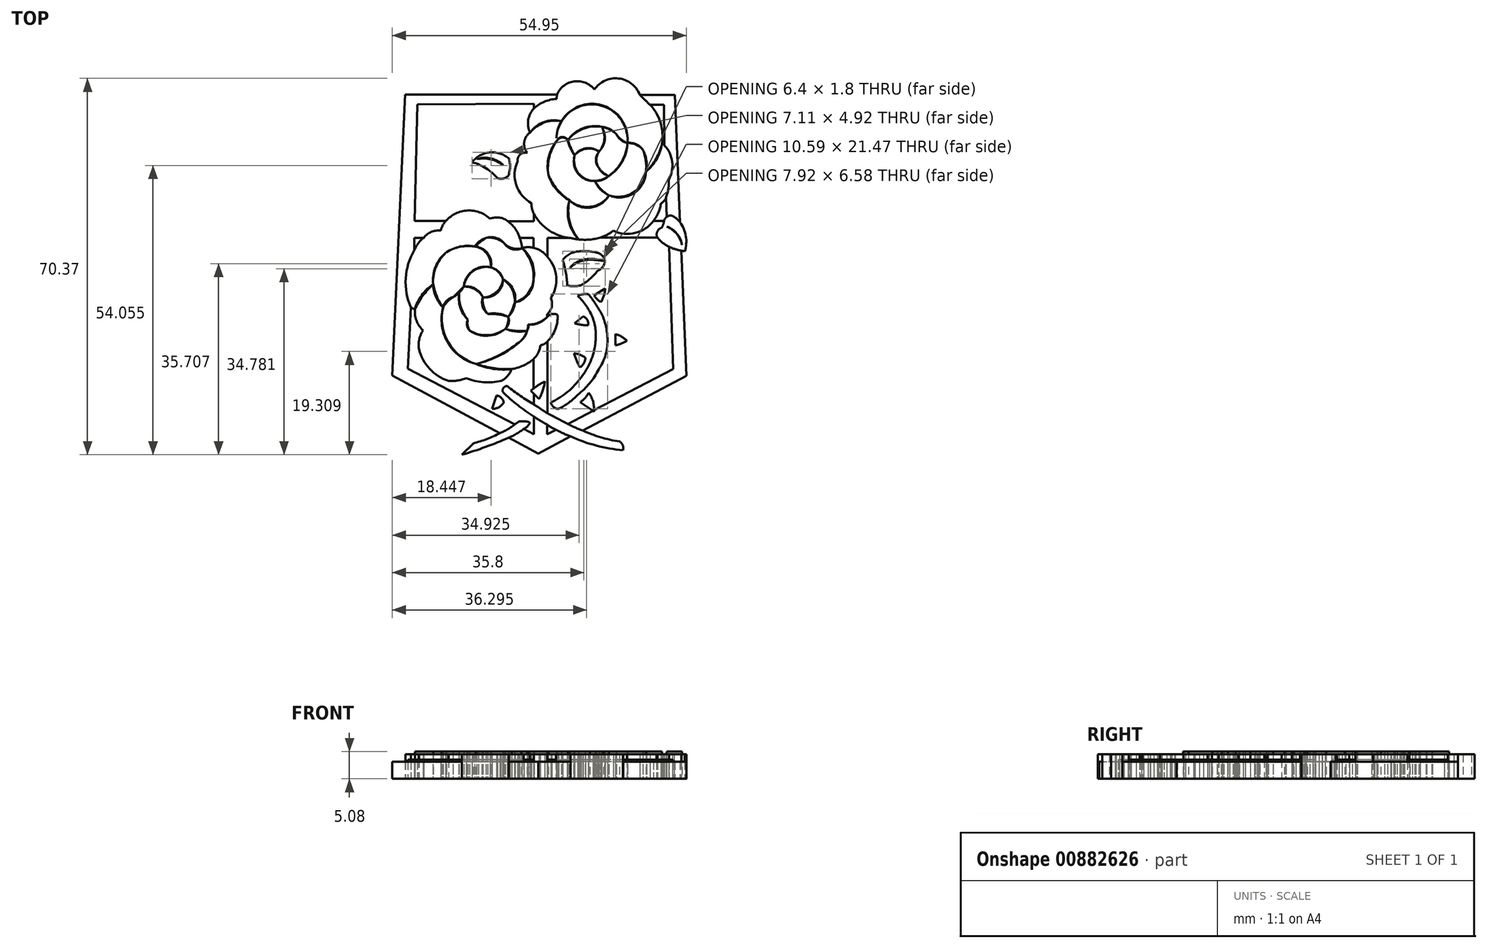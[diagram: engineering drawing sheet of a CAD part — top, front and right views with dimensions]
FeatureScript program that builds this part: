
annotation { "Feature Type Name" : "Feature", "Feature Type Description" : "" }
export const myFeature = defineFeature(function(context is Context, id is Id, definition is map)
    precondition{}
    {
        {
            var Q0;
            Q0=qCreatedBy(makeId("Top.planeOp"),FACE);
            var sketch = newSketch(context, id + "F0", { "sketchPlane" : qUnion([Q0])});
            skLineSegment(sketch, "E0", {"start": v(26.78, -3.75) * mm, "end": v(27.69, -27.16) * mm});
            skLineSegment(sketch, "E1", {"start": v(27.69, -27.16) * mm, "end": v(8.33, -37.36) * mm});
            skLineSegment(sketch, "E2", {"start": v(6.03, -38.47) * mm, "end": v(0, -41.69) * mm});
            skLineSegment(sketch, "E3", {"start": v(0, -41.69) * mm, "end": v(-5.51, -38.69) * mm});
            skLineSegment(sketch, "E4", {"start": v(-7.15, -37.85) * mm, "end": v(-27.26, -27.07) * mm});
            skLineSegment(sketch, "E5", {"start": v(-27.26, -27.07) * mm, "end": v(-24.88, 25.46) * mm});
            skLineSegment(sketch, "E6", {"start": v(-24.88, 25.46) * mm, "end": v(3.53, 25.46) * mm});
            skLineSegment(sketch, "E7", {"start": v(18.98, 25.4) * mm, "end": v(25.53, 25.4) * mm});
            skLineSegment(sketch, "E8", {"start": v(25.53, 25.4) * mm, "end": v(26.49, 1.59) * mm});
            skLineSegment(sketch, "E9", {"start": v(21.57, 1.85) * mm, "end": v(23.52, 1.85) * mm});
            skLineSegment(sketch, "E10", {"start": v(24.05, 2.58) * mm, "end": v(23.9, 6.24) * mm});
            skLineSegment(sketch, "E11", {"start": v(23.5, 23.55) * mm, "end": v(23.6, 15.95) * mm});
            skLineSegment(sketch, "E12", {"start": v(23.5, 23.55) * mm, "end": v(20.94, 23.52) * mm});
            skLineSegment(sketch, "E13", {"start": v(-0.83, 22.84) * mm, "end": v(-0.83, 23.76) * mm});
            skLineSegment(sketch, "E14", {"start": v(-0.83, 23.76) * mm, "end": v(-22.6, 23.6) * mm});
            skLineSegment(sketch, "E15", {"start": v(-22.6, 23.6) * mm, "end": v(-23.11, 1.83) * mm});
            skLineSegment(sketch, "E16", {"start": v(-23.11, 1.83) * mm, "end": v(-17.24, 1.83) * mm});
            skLineSegment(sketch, "E17", {"start": v(-23.15, -3.63) * mm, "end": v(-23.15, -1.32) * mm});
            skLineSegment(sketch, "E18", {"start": v(-23.15, -1.32) * mm, "end": v(-21.4, -1.32) * mm});
            skLineSegment(sketch, "E19", {"start": v(-5.67, 1.77) * mm, "end": v(-0.84, 1.77) * mm});
            skLineSegment(sketch, "E20", {"start": v(-0.84, 1.77) * mm, "end": v(-0.84, 3.19) * mm});
            skLineSegment(sketch, "E21", {"start": v(-3.46, -1.35) * mm, "end": v(-0.86, -1.35) * mm});
            skLineSegment(sketch, "E22", {"start": v(-0.86, -1.35) * mm, "end": v(-0.86, -3.22) * mm});
            skLineSegment(sketch, "E23", {"start": v(1.7, -4.9) * mm, "end": v(1.7, -1.37) * mm});
            skLineSegment(sketch, "E24", {"start": v(1.7, -1.37) * mm, "end": v(6.1, -1.37) * mm});
            skLineSegment(sketch, "E25", {"start": v(11.62, -1.3) * mm, "end": v(22.3, -1.3) * mm});
            skLineSegment(sketch, "E26", {"start": v(24.48, -3) * mm, "end": v(25.26, -25.87) * mm});
            skLineSegment(sketch, "E27", {"start": v(25.26, -25.87) * mm, "end": v(10.43, -33.58) * mm});
            skLineSegment(sketch, "E28", {"start": v(10.23, -33.7) * mm, "end": v(5.57, -36.14) * mm});
            skLineSegment(sketch, "E29", {"start": v(3.32, -37.22) * mm, "end": v(1.68, -38.07) * mm});
            skLineSegment(sketch, "E30", {"start": v(1.68, -38.07) * mm, "end": v(1.68, -36.26) * mm});
            skLineSegment(sketch, "E31", {"start": v(-0.82, -34.75) * mm, "end": v(-0.82, -38.03) * mm});
            skLineSegment(sketch, "E32", {"start": v(-0.82, -38.03) * mm, "end": v(-2.68, -37.02) * mm});
            skLineSegment(sketch, "E33", {"start": v(-4.38, -36.22) * mm, "end": v(-24.37, -25.83) * mm});
            skLineSegment(sketch, "E34", {"start": v(-24.37, -25.83) * mm, "end": v(-23.8, -14.36) * mm});
            skLineSegment(sketch, "E35", {"start": v(1.72, -34.13) * mm, "end": v(1.72, -20.72) * mm});
            skLineSegment(sketch, "E36", {"start": v(-0.84, -24) * mm, "end": v(-0.84, -29.51) * mm});
            skLineSegment(sketch, "E37", {"start": v(-0.8, -30.52) * mm, "end": v(-0.8, -32.5) * mm});
            skArc(sketch, "E38", {"start": v(5.57, -36.14) * mm, "mid": v(6.92, -36.8) * mm, "end": v(8.33, -37.36) * mm});
            skArc(sketch, "E39", {"start": v(3.32, -37.22) * mm, "mid": v(4.67, -37.87) * mm, "end": v(6.03, -38.47) * mm});
            skArc(sketch, "E40", {"start": v(6.03, -38.47) * mm, "mid": v(10.84, -40.16) * mm, "end": v(15.85, -41.06) * mm});
            skArc(sketch, "E41", {"start": v(8.33, -37.36) * mm, "mid": v(11.7, -38.63) * mm, "end": v(15.2, -39.4) * mm});
            skArc(sketch, "E42", {"start": v(15.85, -41.06) * mm, "mid": v(15.8, -40.13) * mm, "end": v(15.2, -39.4) * mm});
            skLineSegment(sketch, "E43", {"start": v(7.86, -32.07) * mm, "end": v(10.23, -33.7) * mm});
            skLineSegment(sketch, "E44", {"start": v(10.23, -33.7) * mm, "end": v(10.44, -33.84) * mm});
            skLineSegment(sketch, "E45", {"start": v(10.44, -33.84) * mm, "end": v(10.43, -33.58) * mm});
            skArc(sketch, "E46", {"start": v(10.43, -33.58) * mm, "mid": v(10.23, -31.85) * mm, "end": v(9.44, -30.29) * mm});
            skArc(sketch, "E47", {"start": v(7.86, -32.07) * mm, "mid": v(8.76, -31.28) * mm, "end": v(9.44, -30.29) * mm});
            skArc(sketch, "E48", {"start": v(22.3, -1.3) * mm, "mid": v(23.29, -2.28) * mm, "end": v(24.48, -3) * mm});
            skArc(sketch, "E49", {"start": v(24.48, -3) * mm, "mid": v(25.6, -3.46) * mm, "end": v(26.78, -3.75) * mm});
            skArc(sketch, "E50", {"start": v(27.4, -3.88) * mm, "mid": v(27.1, -3.8) * mm, "end": v(26.78, -3.75) * mm});
            skArc(sketch, "E51", {"start": v(27.4, -3.88) * mm, "mid": v(27.6, -1.03) * mm, "end": v(26.49, 1.59) * mm});
            skArc(sketch, "E52", {"start": v(25.4, 2.58) * mm, "mid": v(24.72, 2.82) * mm, "end": v(24.05, 2.58) * mm});
            skArc(sketch, "E53", {"start": v(26.49, 1.59) * mm, "mid": v(25.99, 2.14) * mm, "end": v(25.4, 2.58) * mm});
            skArc(sketch, "E54", {"start": v(24.05, 2.58) * mm, "mid": v(23.71, 2.27) * mm, "end": v(23.52, 1.85) * mm});
            skArc(sketch, "E55", {"start": v(23.09, 0.55) * mm, "mid": v(23.37, 1.17) * mm, "end": v(23.52, 1.85) * mm});
            skArc(sketch, "E56", {"start": v(23.09, 0.55) * mm, "mid": v(22.25, -0.18) * mm, "end": v(22.3, -1.3) * mm});
            skArc(sketch, "E57", {"start": v(26.9, -2.71) * mm, "mid": v(25.96, -0.57) * mm, "end": v(24.05, 0.77) * mm});
            skArc(sketch, "E58", {"start": v(1.68, -36.26) * mm, "mid": v(2.47, -36.8) * mm, "end": v(3.32, -37.22) * mm});
            skArc(sketch, "E59", {"start": v(-0.82, -34.75) * mm, "mid": v(0.41, -35.54) * mm, "end": v(1.68, -36.26) * mm});
            skArc(sketch, "E60", {"start": v(-6.6, -30.2) * mm, "mid": v(-3.82, -32.62) * mm, "end": v(-0.82, -34.75) * mm});
            skArc(sketch, "E61", {"start": v(-5.78, -29.05) * mm, "mid": v(-6.5, -29.4) * mm, "end": v(-6.6, -30.2) * mm});
            skArc(sketch, "E62", {"start": v(-5.78, -29.05) * mm, "mid": v(-3.35, -30.88) * mm, "end": v(-0.8, -32.5) * mm});
            skArc(sketch, "E63", {"start": v(1.72, -34.13) * mm, "mid": v(0.47, -33.31) * mm, "end": v(-0.8, -32.5) * mm});
            skArc(sketch, "E64", {"start": v(1.72, -34.13) * mm, "mid": v(3.64, -35.15) * mm, "end": v(5.57, -36.14) * mm});
            skArc(sketch, "E65", {"start": v(-12.12, -39.75) * mm, "mid": v(-9.58, -38.95) * mm, "end": v(-7.15, -37.85) * mm});
            skArc(sketch, "E66", {"start": v(-7.15, -37.85) * mm, "mid": v(-5.7, -37.13) * mm, "end": v(-4.38, -36.22) * mm});
            skArc(sketch, "E67", {"start": v(-4.38, -36.22) * mm, "mid": v(-4, -35.95) * mm, "end": v(-3.61, -35.67) * mm});
            skArc(sketch, "E68", {"start": v(-5.51, -38.69) * mm, "mid": v(-4.04, -37.96) * mm, "end": v(-2.68, -37.02) * mm});
            skArc(sketch, "E69", {"start": v(-14.26, -41.89) * mm, "mid": v(-9.83, -40.43) * mm, "end": v(-5.51, -38.69) * mm});
            skLineSegment(sketch, "E70", {"start": v(-12.12, -39.75) * mm, "end": v(-14.26, -41.89) * mm});
            skLineSegment(sketch, "E71", {"start": v(-3.61, -35.67) * mm, "end": v(-2.28, -35.67) * mm});
            skArc(sketch, "E72", {"start": v(-2.68, -37.02) * mm, "mid": v(-2, -36.58) * mm, "end": v(-1.55, -35.9) * mm});
            skArc(sketch, "E73", {"start": v(-1.55, -35.9) * mm, "mid": v(-1.9, -35.73) * mm, "end": v(-2.28, -35.67) * mm});
            skArc(sketch, "E74", {"start": v(1.24, -28.18) * mm, "mid": v(0.16, -28.8) * mm, "end": v(-0.84, -29.51) * mm});
            skLineSegment(sketch, "E75", {"start": v(-0.84, -29.51) * mm, "end": v(-1.36, -29.92) * mm});
            skLineSegment(sketch, "E76", {"start": v(-1.36, -29.92) * mm, "end": v(-0.8, -30.52) * mm});
            skLineSegment(sketch, "E77", {"start": v(-0.8, -30.52) * mm, "end": v(0.16, -31.43) * mm});
            skArc(sketch, "E78", {"start": v(0.16, -31.43) * mm, "mid": v(0.87, -29.86) * mm, "end": v(1.24, -28.18) * mm});
            skArc(sketch, "E79", {"start": v(2.37, -32.1) * mm, "mid": v(5.48, -30.14) * mm, "end": v(8, -27.45) * mm});
            skArc(sketch, "E80", {"start": v(8, -27.45) * mm, "mid": v(9.8, -24.46) * mm, "end": v(10.67, -21.09) * mm});
            skArc(sketch, "E81", {"start": v(10.67, -21.09) * mm, "mid": v(10.73, -18.72) * mm, "end": v(10.23, -16.41) * mm});
            skArc(sketch, "E82", {"start": v(10.23, -16.41) * mm, "mid": v(9.04, -14.12) * mm, "end": v(7.38, -12.15) * mm});
            skArc(sketch, "E83", {"start": v(9.43, -11.89) * mm, "mid": v(8.38, -11.87) * mm, "end": v(7.38, -12.15) * mm});
            skArc(sketch, "E84", {"start": v(11.9, -15.64) * mm, "mid": v(10.72, -13.72) * mm, "end": v(9.43, -11.89) * mm});
            skArc(sketch, "E85", {"start": v(12.96, -20.1) * mm, "mid": v(12.64, -17.82) * mm, "end": v(11.9, -15.64) * mm});
            skArc(sketch, "E86", {"start": v(11.34, -25.9) * mm, "mid": v(12.61, -23.13) * mm, "end": v(12.96, -20.1) * mm});
            skArc(sketch, "E87", {"start": v(7.38, -30.66) * mm, "mid": v(9.64, -28.52) * mm, "end": v(11.34, -25.9) * mm});
            skArc(sketch, "E88", {"start": v(3.84, -33.32) * mm, "mid": v(5.72, -32.15) * mm, "end": v(7.38, -30.66) * mm});
            skArc(sketch, "E89", {"start": v(2.37, -32.1) * mm, "mid": v(2.88, -32.97) * mm, "end": v(3.84, -33.32) * mm});
            skArc(sketch, "E90", {"start": v(7.8, -25.56) * mm, "mid": v(8.53, -24.78) * mm, "end": v(8.85, -23.77) * mm});
            skArc(sketch, "E91", {"start": v(8.85, -23.77) * mm, "mid": v(7.84, -23.2) * mm, "end": v(6.7, -22.96) * mm});
            skArc(sketch, "E92", {"start": v(6.7, -22.96) * mm, "mid": v(7.17, -24.3) * mm, "end": v(7.8, -25.56) * mm});
            skLineSegment(sketch, "E93", {"start": v(14.42, -19.33) * mm, "end": v(14.42, -21.43) * mm});
            skArc(sketch, "E94", {"start": v(14.42, -21.43) * mm, "mid": v(15.54, -21.11) * mm, "end": v(16.57, -20.58) * mm});
            skArc(sketch, "E95", {"start": v(16.57, -20.58) * mm, "mid": v(15.58, -19.81) * mm, "end": v(14.42, -19.33) * mm});
            skArc(sketch, "E96", {"start": v(9.34, -17.66) * mm, "mid": v(9.18, -16.66) * mm, "end": v(8.38, -16.03) * mm});
            skArc(sketch, "E97", {"start": v(6.8, -17.3) * mm, "mid": v(8.05, -17.6) * mm, "end": v(9.34, -17.66) * mm});
            skLineSegment(sketch, "E98", {"start": v(6.8, -17.3) * mm, "end": v(8.38, -16.03) * mm});
            skLineSegment(sketch, "E99", {"start": v(10.46, -12.07) * mm, "end": v(12.51, -10.79) * mm});
            skArc(sketch, "E100", {"start": v(11.73, -13.37) * mm, "mid": v(12.29, -12.13) * mm, "end": v(12.51, -10.79) * mm});
            skArc(sketch, "E101", {"start": v(10.46, -12.07) * mm, "mid": v(11, -12.81) * mm, "end": v(11.73, -13.37) * mm});
            skArc(sketch, "E102", {"start": v(6.1, -1.37) * mm, "mid": v(8.86, -1.7) * mm, "end": v(11.62, -1.3) * mm});
            skArc(sketch, "E103", {"start": v(5.44, -10.23) * mm, "mid": v(5.18, -7.83) * mm, "end": v(4.58, -5.5) * mm});
            skArc(sketch, "E104", {"start": v(5.44, -10.23) * mm, "mid": v(6.66, -10.4) * mm, "end": v(7.9, -10.23) * mm});
            skArc(sketch, "E105", {"start": v(7.9, -10.23) * mm, "mid": v(9.63, -9.07) * mm, "end": v(11.05, -7.54) * mm});
            skArc(sketch, "E106", {"start": v(11.05, -7.54) * mm, "mid": v(12.04, -6.8) * mm, "end": v(12.5, -5.66) * mm});
            skArc(sketch, "E107", {"start": v(12.5, -5.66) * mm, "mid": v(12, -4.7) * mm, "end": v(11.05, -4.14) * mm});
            skArc(sketch, "E108", {"start": v(7.61, -3.88) * mm, "mid": v(5.9, -4.34) * mm, "end": v(4.58, -5.5) * mm});
            skArc(sketch, "E109", {"start": v(11.05, -4.14) * mm, "mid": v(9.35, -3.84) * mm, "end": v(7.61, -3.88) * mm});
            skArc(sketch, "E110", {"start": v(-3, -3.26) * mm, "mid": v(-3.18, -2.3) * mm, "end": v(-3.46, -1.35) * mm});
            skArc(sketch, "E111", {"start": v(-0.83, 22.84) * mm, "mid": v(-1.86, 20.7) * mm, "end": v(-1.52, 18.34) * mm});
            skArc(sketch, "E112", {"start": v(-1.52, 18.34) * mm, "mid": v(-2.6, 16.56) * mm, "end": v(-2.03, 14.55) * mm});
            skArc(sketch, "E113", {"start": v(-2.03, 14.55) * mm, "mid": v(-3.37, 14.24) * mm, "end": v(-3.84, 12.95) * mm});
            skArc(sketch, "E114", {"start": v(-3.84, 12.95) * mm, "mid": v(-4.1, 8.53) * mm, "end": v(-1.25, 5.14) * mm});
            skArc(sketch, "E115", {"start": v(-1.25, 5.14) * mm, "mid": v(-1.16, 4.14) * mm, "end": v(-0.84, 3.19) * mm});
            skArc(sketch, "E116", {"start": v(-5.67, 1.77) * mm, "mid": v(-7.27, 2.45) * mm, "end": v(-9, 2.23) * mm});
            skArc(sketch, "E117", {"start": v(-9, 2.23) * mm, "mid": v(-13.2, 3.77) * mm, "end": v(-17.24, 1.83) * mm});
            skArc(sketch, "E118", {"start": v(-17.24, 1.83) * mm, "mid": v(-17.86, 0.98) * mm, "end": v(-18.22, 0) * mm});
            skArc(sketch, "E119", {"start": v(-18.22, 0) * mm, "mid": v(-19.99, -0.23) * mm, "end": v(-21.4, -1.32) * mm});
            skArc(sketch, "E120", {"start": v(-21.4, -1.32) * mm, "mid": v(-22.42, -2.37) * mm, "end": v(-23.15, -3.63) * mm});
            skArc(sketch, "E121", {"start": v(-23.15, -3.63) * mm, "mid": v(-24.76, -8.92) * mm, "end": v(-23.8, -14.36) * mm});
            skArc(sketch, "E122", {"start": v(3.44, 24.64) * mm, "mid": v(1.15, 24.1) * mm, "end": v(-0.83, 22.84) * mm});
            skArc(sketch, "E123", {"start": v(3.44, 24.64) * mm, "mid": v(3.48, 25.05) * mm, "end": v(3.53, 25.46) * mm});
            skArc(sketch, "E124", {"start": v(10.52, 26.37) * mm, "mid": v(6.76, 27.9) * mm, "end": v(3.53, 25.46) * mm});
            skArc(sketch, "E125", {"start": v(18.98, 25.4) * mm, "mid": v(15.04, 28.45) * mm, "end": v(10.52, 26.37) * mm});
            skArc(sketch, "E126", {"start": v(18.98, 25.4) * mm, "mid": v(19.94, 24.44) * mm, "end": v(20.94, 23.52) * mm});
            skArc(sketch, "E127", {"start": v(20.13, 11.01) * mm, "mid": v(23.23, 17.1) * mm, "end": v(20.94, 23.52) * mm});
            skArc(sketch, "E128", {"start": v(23.6, 15.95) * mm, "mid": v(23.4, 16.15) * mm, "end": v(23.13, 16.28) * mm});
            skArc(sketch, "E129", {"start": v(24.4, 9.53) * mm, "mid": v(25.04, 12.87) * mm, "end": v(23.6, 15.95) * mm});
            skArc(sketch, "E130", {"start": v(23.9, 6.24) * mm, "mid": v(24.34, 7.85) * mm, "end": v(24.4, 9.53) * mm});
            skArc(sketch, "E131", {"start": v(22.95, 5.07) * mm, "mid": v(23.54, 5.56) * mm, "end": v(23.9, 6.24) * mm});
            skArc(sketch, "E132", {"start": v(21.57, 1.85) * mm, "mid": v(22.46, 3.37) * mm, "end": v(22.95, 5.07) * mm});
            skArc(sketch, "E133", {"start": v(14.04, 0) * mm, "mid": v(18.14, -0.43) * mm, "end": v(21.57, 1.85) * mm});
            skArc(sketch, "E134", {"start": v(11.62, -1.3) * mm, "mid": v(12.9, -0.77) * mm, "end": v(14.04, 0) * mm});
            skArc(sketch, "E135", {"start": v(-0.84, 3.19) * mm, "mid": v(2.06, 0.03) * mm, "end": v(6.1, -1.37) * mm});
            skArc(sketch, "E136", {"start": v(10.6, 9.29) * mm, "mid": v(16.07, 6.28) * mm, "end": v(20.13, 11.01) * mm});
            skArc(sketch, "E137", {"start": v(5.86, 5.67) * mm, "mid": v(9.79, 4.31) * mm, "end": v(13.25, 6.6) * mm});
            skArc(sketch, "E138", {"start": v(5.86, 5.67) * mm, "mid": v(5.73, 1.77) * mm, "end": v(7.6, -1.65) * mm});
            skArc(sketch, "E139", {"start": v(20.13, 11.01) * mm, "mid": v(20.22, 13.1) * mm, "end": v(19.59, 15.08) * mm});
            skArc(sketch, "E140", {"start": v(19.59, 15.08) * mm, "mid": v(18.32, 16.14) * mm, "end": v(16.68, 16.4) * mm});
            skArc(sketch, "E141", {"start": v(14.6, 18.07) * mm, "mid": v(15.44, 16.98) * mm, "end": v(16.68, 16.4) * mm});
            skArc(sketch, "E142", {"start": v(14.6, 18.07) * mm, "mid": v(9.8, 19.5) * mm, "end": v(5.52, 16.9) * mm});
            skArc(sketch, "E143", {"start": v(16.68, 16.4) * mm, "mid": v(10.5, 23.7) * mm, "end": v(3.4, 17.3) * mm});
            skArc(sketch, "E144", {"start": v(5.52, 16.9) * mm, "mid": v(4.54, 17.41) * mm, "end": v(3.57, 16.9) * mm});
            skArc(sketch, "E145", {"start": v(3.4, 17.3) * mm, "mid": v(3.44, 17.08) * mm, "end": v(3.57, 16.9) * mm});
            skArc(sketch, "E146", {"start": v(3.57, 16.9) * mm, "mid": v(2.1, 13.82) * mm, "end": v(1.91, 10.41) * mm});
            skArc(sketch, "E147", {"start": v(1.91, 10.41) * mm, "mid": v(3.53, 7.75) * mm, "end": v(5.86, 5.67) * mm});
            skArc(sketch, "E148", {"start": v(5.52, 16.9) * mm, "mid": v(6.12, 15.45) * mm, "end": v(6.82, 14.05) * mm});
            skArc(sketch, "E149", {"start": v(11.36, 14.76) * mm, "mid": v(8.94, 15.4) * mm, "end": v(6.82, 14.05) * mm});
            skArc(sketch, "E150", {"start": v(11.36, 14.76) * mm, "mid": v(12.46, 17) * mm, "end": v(11.85, 19.43) * mm});
            skArc(sketch, "E151", {"start": v(11.36, 14.76) * mm, "mid": v(10.8, 13.23) * mm, "end": v(11.36, 11.7) * mm});
            skArc(sketch, "E152", {"start": v(11.36, 11.7) * mm, "mid": v(12.17, 10.82) * mm, "end": v(13.2, 10.23) * mm});
            skArc(sketch, "E153", {"start": v(13.2, 10.23) * mm, "mid": v(15.7, 12.88) * mm, "end": v(16.68, 16.4) * mm});
            skArc(sketch, "E154", {"start": v(10.6, 9.29) * mm, "mid": v(11.98, 9.57) * mm, "end": v(13.2, 10.23) * mm});
            skArc(sketch, "E155", {"start": v(6.82, 14.05) * mm, "mid": v(7.46, 10.67) * mm, "end": v(10.6, 9.29) * mm});
            skArc(sketch, "E156", {"start": v(4.35, 20.49) * mm, "mid": v(1.13, 20.2) * mm, "end": v(-1.52, 18.34) * mm});
            skArc(sketch, "E157", {"start": v(-7.58, 9.82) * mm, "mid": v(-9.76, 11.66) * mm, "end": v(-12.37, 12.8) * mm});
            skArc(sketch, "E158", {"start": v(-5.44, 13.45) * mm, "mid": v(-9.04, 14.62) * mm, "end": v(-12.37, 12.8) * mm});
            skArc(sketch, "E159", {"start": v(-5.6, 10.22) * mm, "mid": v(-5.26, 11.82) * mm, "end": v(-5.44, 13.45) * mm});
            skArc(sketch, "E160", {"start": v(-7.58, 9.82) * mm, "mid": v(-6.54, 9.74) * mm, "end": v(-5.6, 10.22) * mm});
            skArc(sketch, "E161", {"start": v(-3.46, -1.35) * mm, "mid": v(-4.31, 0.39) * mm, "end": v(-5.67, 1.77) * mm});
            skArc(sketch, "E162", {"start": v(-0.86, -3.22) * mm, "mid": v(-1.93, -3.07) * mm, "end": v(-3, -3.26) * mm});
            skArc(sketch, "E163", {"start": v(1.7, -4.9) * mm, "mid": v(0.58, -3.82) * mm, "end": v(-0.86, -3.22) * mm});
            skArc(sketch, "E164", {"start": v(2.35, -12.62) * mm, "mid": v(3.36, -8.65) * mm, "end": v(1.7, -4.9) * mm});
            skArc(sketch, "E165", {"start": v(1.7, -15.57) * mm, "mid": v(2.54, -14.2) * mm, "end": v(2.35, -12.62) * mm});
            skArc(sketch, "E166", {"start": v(1.72, -20.72) * mm, "mid": v(3.2, -18.45) * mm, "end": v(3.64, -15.78) * mm});
            skArc(sketch, "E167", {"start": v(0.4, -21.42) * mm, "mid": v(1.12, -21.19) * mm, "end": v(1.72, -20.72) * mm});
            skArc(sketch, "E168", {"start": v(-0.84, -24) * mm, "mid": v(0, -22.82) * mm, "end": v(0.4, -21.42) * mm});
            skArc(sketch, "E169", {"start": v(-4.96, -25.89) * mm, "mid": v(-2.78, -25.21) * mm, "end": v(-0.84, -24) * mm});
            skArc(sketch, "E170", {"start": v(-6.94, -28.1) * mm, "mid": v(-5.74, -27.18) * mm, "end": v(-4.96, -25.89) * mm});
            skArc(sketch, "E171", {"start": v(-13.45, -27.58) * mm, "mid": v(-10.23, -28.33) * mm, "end": v(-6.94, -28.1) * mm});
            skArc(sketch, "E172", {"start": v(-16.76, -28.1) * mm, "mid": v(-15.08, -28.01) * mm, "end": v(-13.45, -27.58) * mm});
            skArc(sketch, "E173", {"start": v(-22.29, -22.15) * mm, "mid": v(-20.28, -25.82) * mm, "end": v(-16.76, -28.1) * mm});
            skArc(sketch, "E174", {"start": v(-21.54, -18.62) * mm, "mid": v(-22.23, -20.32) * mm, "end": v(-22.29, -22.15) * mm});
            skArc(sketch, "E175", {"start": v(-23.04, -14.72) * mm, "mid": v(-22.73, -16.84) * mm, "end": v(-21.54, -18.62) * mm});
            skArc(sketch, "E176", {"start": v(-23.04, -14.72) * mm, "mid": v(-23.41, -14.54) * mm, "end": v(-23.8, -14.36) * mm});
            skArc(sketch, "E177", {"start": v(-19.6, -10.07) * mm, "mid": v(-21.77, -12.07) * mm, "end": v(-23.04, -14.72) * mm});
            skArc(sketch, "E178", {"start": v(-19.6, -10.07) * mm, "mid": v(-19.11, -12.4) * mm, "end": v(-17.78, -14.36) * mm});
            skArc(sketch, "E179", {"start": v(-17.1, -4) * mm, "mid": v(-19.09, -6.73) * mm, "end": v(-19.6, -10.07) * mm});
            skArc(sketch, "E180", {"start": v(-11.15, -3.1) * mm, "mid": v(-14.2, -2.96) * mm, "end": v(-17.1, -4) * mm});
            skArc(sketch, "E181", {"start": v(-8.84, -6.87) * mm, "mid": v(-9.38, -4.61) * mm, "end": v(-11.15, -3.1) * mm});
            skArc(sketch, "E182", {"start": v(-9.74, -1.34) * mm, "mid": v(-10.94, -1.98) * mm, "end": v(-11.87, -2.96) * mm});
            skArc(sketch, "E183", {"start": v(-6.4, -2.3) * mm, "mid": v(-7.97, -1.48) * mm, "end": v(-9.74, -1.34) * mm});
            skArc(sketch, "E184", {"start": v(-6.4, -2.3) * mm, "mid": v(-4.83, -3.27) * mm, "end": v(-3, -3.26) * mm});
            skArc(sketch, "E185", {"start": v(-0.85, -9.13) * mm, "mid": v(-1.15, -5.91) * mm, "end": v(-3, -3.26) * mm});
            skArc(sketch, "E186", {"start": v(-4.37, -13.41) * mm, "mid": v(-1.84, -11.9) * mm, "end": v(-0.85, -9.13) * mm});
            skArc(sketch, "E187", {"start": v(-4.37, -13.41) * mm, "mid": v(-4.89, -10.97) * mm, "end": v(-6.58, -9.13) * mm});
            skArc(sketch, "E188", {"start": v(-6.58, -9.13) * mm, "mid": v(-7.45, -7.73) * mm, "end": v(-8.84, -6.87) * mm});
            skArc(sketch, "E189", {"start": v(-8.84, -6.87) * mm, "mid": v(-12.16, -7.56) * mm, "end": v(-13.9, -10.46) * mm});
            skArc(sketch, "E190", {"start": v(-10.33, -12.45) * mm, "mid": v(-7.7, -11.65) * mm, "end": v(-6.58, -9.13) * mm});
            skArc(sketch, "E191", {"start": v(-10.33, -12.45) * mm, "mid": v(-11.84, -10.96) * mm, "end": v(-13.9, -10.46) * mm});
            skArc(sketch, "E192", {"start": v(-15.93, -12.45) * mm, "mid": v(-17.14, -13.13) * mm, "end": v(-17.78, -14.36) * mm});
            skArc(sketch, "E193", {"start": v(-15.93, -12.45) * mm, "mid": v(-14.77, -11.6) * mm, "end": v(-13.9, -10.46) * mm});
            skArc(sketch, "E194", {"start": v(-17.78, -14.36) * mm, "mid": v(-16.9, -20.94) * mm, "end": v(-11.6, -24.93) * mm});
            skArc(sketch, "E195", {"start": v(-11.6, -24.93) * mm, "mid": v(-8.32, -25.7) * mm, "end": v(-4.96, -25.89) * mm});
            skArc(sketch, "E196", {"start": v(-11.6, -24.93) * mm, "mid": v(-7.13, -23.19) * mm, "end": v(-3.16, -20.5) * mm});
            skArc(sketch, "E197", {"start": v(-3.16, -20.5) * mm, "mid": v(-2.23, -19.16) * mm, "end": v(-1.86, -17.58) * mm});
            skArc(sketch, "E198", {"start": v(-1.86, -17.58) * mm, "mid": v(0.07, -17.18) * mm, "end": v(1.72, -16.1) * mm});
            skArc(sketch, "E199", {"start": v(1.7, -15.57) * mm, "mid": v(1.68, -15.84) * mm, "end": v(1.72, -16.1) * mm});
            skArc(sketch, "E200", {"start": v(3.64, -15.78) * mm, "mid": v(2.62, -15.57) * mm, "end": v(1.72, -16.1) * mm});
            skArc(sketch, "E201", {"start": v(-6.13, -18.35) * mm, "mid": v(-4.12, -18.84) * mm, "end": v(-2.06, -18.7) * mm});
            skArc(sketch, "E202", {"start": v(-5.6, -16.1) * mm, "mid": v(-4.75, -14.87) * mm, "end": v(-4.37, -13.41) * mm});
            skArc(sketch, "E203", {"start": v(-6.13, -18.35) * mm, "mid": v(-5.66, -17.28) * mm, "end": v(-5.6, -16.1) * mm});
            skArc(sketch, "E204", {"start": v(-5.6, -16.1) * mm, "mid": v(-7.49, -15.65) * mm, "end": v(-9.42, -15.57) * mm});
            skArc(sketch, "E205", {"start": v(-10.33, -12.45) * mm, "mid": v(-10.22, -14.1) * mm, "end": v(-9.42, -15.57) * mm});
            skArc(sketch, "E206", {"start": v(-12.8, -18.69) * mm, "mid": v(-9.4, -19.65) * mm, "end": v(-6.13, -18.35) * mm});
            skArc(sketch, "E207", {"start": v(-13.15, -16.63) * mm, "mid": v(-13.19, -17.7) * mm, "end": v(-12.8, -18.69) * mm});
            skArc(sketch, "E208", {"start": v(-14.77, -11.6) * mm, "mid": v(-14.58, -14.32) * mm, "end": v(-13.15, -16.63) * mm});
            skArc(sketch, "E209", {"start": v(-6.45, -32.13) * mm, "mid": v(-6.9, -31.24) * mm, "end": v(-7.8, -30.82) * mm});
            skArc(sketch, "E210", {"start": v(-8.6, -33.3) * mm, "mid": v(-7.36, -33.01) * mm, "end": v(-6.45, -32.13) * mm});
            skLineSegment(sketch, "E211", {"start": v(-7.8, -30.82) * mm, "end": v(-8.6, -33.3) * mm});
            skArc(sketch, "E212", {"start": v(16.68, 16.4) * mm, "mid": v(10.5, 23.59) * mm, "end": v(3.4, 17.3) * mm});
            skArc(sketch, "E213", {"start": v(14.6, 18.07) * mm, "mid": v(15.49, 17.04) * mm, "end": v(16.68, 16.4) * mm});
            skArc(sketch, "E214", {"start": v(14.6, 18.07) * mm, "mid": v(13.35, 19) * mm, "end": v(11.85, 19.43) * mm});
            skArc(sketch, "E215", {"start": v(11.36, 14.76) * mm, "mid": v(12.36, 17.02) * mm, "end": v(11.85, 19.43) * mm});
            skArc(sketch, "E216", {"start": v(11.85, 19.43) * mm, "mid": v(8.35, 19) * mm, "end": v(5.52, 16.9) * mm});
            skArc(sketch, "E217", {"start": v(5.52, 16.9) * mm, "mid": v(6.03, 15.41) * mm, "end": v(6.82, 14.05) * mm});
            skArc(sketch, "E218", {"start": v(11.36, 14.76) * mm, "mid": v(8.95, 15.31) * mm, "end": v(6.82, 14.05) * mm});
            skArc(sketch, "E219", {"start": v(11.36, 14.76) * mm, "mid": v(10.87, 13.23) * mm, "end": v(11.36, 11.7) * mm});
            skArc(sketch, "E220", {"start": v(11.36, 11.7) * mm, "mid": v(12.12, 10.76) * mm, "end": v(13.2, 10.23) * mm});
            skArc(sketch, "E221", {"start": v(13.2, 10.23) * mm, "mid": v(15.64, 12.92) * mm, "end": v(16.68, 16.4) * mm});
            skArc(sketch, "E222", {"start": v(10.6, 9.29) * mm, "mid": v(12, 9.5) * mm, "end": v(13.2, 10.23) * mm});
            skArc(sketch, "E223", {"start": v(6.82, 14.05) * mm, "mid": v(7.54, 10.74) * mm, "end": v(10.6, 9.29) * mm});
            skArc(sketch, "E224", {"start": v(19.59, 15.08) * mm, "mid": v(18.28, 16.07) * mm, "end": v(16.68, 16.4) * mm});
            skArc(sketch, "E225", {"start": v(20.13, 11.01) * mm, "mid": v(20.12, 13.08) * mm, "end": v(19.59, 15.08) * mm});
            skArc(sketch, "E226", {"start": v(20.13, 11.01) * mm, "mid": v(22.03, 13.42) * mm, "end": v(23.13, 16.28) * mm});
            skArc(sketch, "E227", {"start": v(13.25, 6.6) * mm, "mid": v(17.75, 7.15) * mm, "end": v(20.13, 11.01) * mm});
            skArc(sketch, "E228", {"start": v(10.6, 9.29) * mm, "mid": v(11.74, 7.76) * mm, "end": v(13.25, 6.6) * mm});
            skArc(sketch, "E229", {"start": v(5.86, 5.67) * mm, "mid": v(9.77, 4.46) * mm, "end": v(13.25, 6.6) * mm});
            skArc(sketch, "E230", {"start": v(1.91, 10.41) * mm, "mid": v(3.43, 7.66) * mm, "end": v(5.86, 5.67) * mm});
            skArc(sketch, "E231", {"start": v(3.57, 16.9) * mm, "mid": v(1.98, 13.85) * mm, "end": v(1.91, 10.41) * mm});
            skArc(sketch, "E232", {"start": v(5.52, 16.9) * mm, "mid": v(4.54, 17.54) * mm, "end": v(3.57, 16.9) * mm});
            skArc(sketch, "E233", {"start": v(4.35, 20.49) * mm, "mid": v(1.09, 20.3) * mm, "end": v(-1.52, 18.34) * mm});
            skArc(sketch, "E234", {"start": v(5.86, 5.67) * mm, "mid": v(5.86, 1.8) * mm, "end": v(7.6, -1.65) * mm});
            skArc(sketch, "E235", {"start": v(26.9, -2.71) * mm, "mid": v(25.9, -0.62) * mm, "end": v(24.05, 0.77) * mm});
            skArc(sketch, "E236", {"start": v(-1.86, -17.58) * mm, "mid": v(0.1, -17.25) * mm, "end": v(1.72, -16.1) * mm});
            skArc(sketch, "E237", {"start": v(-6.13, -18.35) * mm, "mid": v(-4.12, -18.75) * mm, "end": v(-2.06, -18.7) * mm});
            skArc(sketch, "E238", {"start": v(-2.06, -18.7) * mm, "mid": v(-1.85, -18.16) * mm, "end": v(-1.86, -17.58) * mm});
            skArc(sketch, "E239", {"start": v(-3.16, -20.5) * mm, "mid": v(-2.46, -19.7) * mm, "end": v(-2.06, -18.7) * mm});
            skArc(sketch, "E240", {"start": v(-11.6, -24.93) * mm, "mid": v(-7.09, -23.27) * mm, "end": v(-3.16, -20.5) * mm});
            skArc(sketch, "E241", {"start": v(-11.6, -24.93) * mm, "mid": v(-8.34, -25.84) * mm, "end": v(-4.96, -25.89) * mm});
            skArc(sketch, "E242", {"start": v(-17.78, -14.36) * mm, "mid": v(-16.8, -20.87) * mm, "end": v(-11.6, -24.93) * mm});
            skArc(sketch, "E243", {"start": v(-19.6, -10.07) * mm, "mid": v(-21.6, -12.2) * mm, "end": v(-23.04, -14.72) * mm});
            skArc(sketch, "E244", {"start": v(-19.6, -10.07) * mm, "mid": v(-18.93, -12.31) * mm, "end": v(-17.78, -14.36) * mm});
            skArc(sketch, "E245", {"start": v(-15.93, -12.45) * mm, "mid": v(-16.98, -13.28) * mm, "end": v(-17.78, -14.36) * mm});
            skArc(sketch, "E246", {"start": v(-14.77, -11.6) * mm, "mid": v(-14.46, -14.28) * mm, "end": v(-13.15, -16.63) * mm});
            skArc(sketch, "E247", {"start": v(-15.93, -12.45) * mm, "mid": v(-14.9, -11.47) * mm, "end": v(-13.9, -10.46) * mm});
            skArc(sketch, "E248", {"start": v(-13.15, -16.63) * mm, "mid": v(-13.3, -17.72) * mm, "end": v(-12.8, -18.69) * mm});
            skArc(sketch, "E249", {"start": v(-12.8, -18.69) * mm, "mid": v(-9.41, -19.54) * mm, "end": v(-6.13, -18.35) * mm});
            skArc(sketch, "E250", {"start": v(-6.13, -18.35) * mm, "mid": v(-5.52, -17.31) * mm, "end": v(-5.6, -16.1) * mm});
            skArc(sketch, "E251", {"start": v(-5.6, -16.1) * mm, "mid": v(-7.47, -15.52) * mm, "end": v(-9.42, -15.57) * mm});
            skArc(sketch, "E252", {"start": v(-10.33, -12.45) * mm, "mid": v(-10.4, -14.15) * mm, "end": v(-9.43, -15.55) * mm});
            skArc(sketch, "E253", {"start": v(-10.33, -12.45) * mm, "mid": v(-11.77, -10.84) * mm, "end": v(-13.9, -10.46) * mm});
            skArc(sketch, "E254", {"start": v(-10.33, -12.45) * mm, "mid": v(-7.81, -11.51) * mm, "end": v(-6.58, -9.13) * mm});
            skArc(sketch, "E255", {"start": v(-5.6, -16.1) * mm, "mid": v(-4.87, -14.81) * mm, "end": v(-4.37, -13.41) * mm});
            skArc(sketch, "E256", {"start": v(-4.37, -13.41) * mm, "mid": v(-4.72, -10.88) * mm, "end": v(-6.58, -9.13) * mm});
            skArc(sketch, "E257", {"start": v(-4.37, -13.41) * mm, "mid": v(-1.96, -11.8) * mm, "end": v(-0.85, -9.13) * mm});
            skArc(sketch, "E258", {"start": v(-0.85, -9.13) * mm, "mid": v(-1.3, -5.97) * mm, "end": v(-3, -3.26) * mm});
            skArc(sketch, "E259", {"start": v(-6.4, -2.3) * mm, "mid": v(-4.88, -3.45) * mm, "end": v(-3, -3.26) * mm});
            skArc(sketch, "E260", {"start": v(-6.4, -2.3) * mm, "mid": v(-7.92, -1.32) * mm, "end": v(-9.74, -1.34) * mm});
            skArc(sketch, "E261", {"start": v(-9.74, -1.34) * mm, "mid": v(-10.83, -2.12) * mm, "end": v(-11.87, -2.96) * mm});
            skArc(sketch, "E262", {"start": v(-8.84, -6.87) * mm, "mid": v(-9.24, -4.53) * mm, "end": v(-11.15, -3.1) * mm});
            skArc(sketch, "E263", {"start": v(-11.15, -3.1) * mm, "mid": v(-11.48, -2.89) * mm, "end": v(-11.87, -2.96) * mm});
            skArc(sketch, "E264", {"start": v(-11.87, -2.96) * mm, "mid": v(-14.58, -2.97) * mm, "end": v(-17.1, -4) * mm});
            skArc(sketch, "E265", {"start": v(-17.09, -4.01) * mm, "mid": v(-19.17, -6.7) * mm, "end": v(-19.6, -10.07) * mm});
            skArc(sketch, "E266", {"start": v(-6.58, -9.13) * mm, "mid": v(-7.38, -7.67) * mm, "end": v(-8.84, -6.87) * mm});
            skArc(sketch, "E267", {"start": v(-8.84, -6.87) * mm, "mid": v(-12.2, -7.48) * mm, "end": v(-13.9, -10.46) * mm});
            skArc(sketch, "E268", {"start": v(9.7, -5.44) * mm, "mid": v(7.6, -5.85) * mm, "end": v(5.84, -7.08) * mm});
            skArc(sketch, "E269", {"start": v(12.23, -5.66) * mm, "mid": v(10.97, -5.48) * mm, "end": v(9.7, -5.44) * mm});
            skArc(sketch, "E270", {"start": v(8.77, -5.36) * mm, "mid": v(7.12, -5.9) * mm, "end": v(5.84, -7.08) * mm});
            skArc(sketch, "E271", {"start": v(12.23, -5.66) * mm, "mid": v(10.52, -5.3) * mm, "end": v(8.77, -5.36) * mm});
            skArc(sketch, "E272", {"start": v(-6.53, 12.22) * mm, "mid": v(-8.88, 13.34) * mm, "end": v(-11.48, 13.36) * mm});
            skArc(sketch, "E273", {"start": v(-6.53, 12.22) * mm, "mid": v(-8.84, 13.52) * mm, "end": v(-11.48, 13.36) * mm});
            skSolve(sketch);
        }
        {
            var Q0;
            Q0=makeQuery(id+"F0.imprint","IMPRINT",FACE,{"disambiguationData":[TD([[makeQuery(id+"F0.imprint","IMPRINT",EDGE,{"derivedFrom":sQuery(id+"F0.wireOp",EDGE,"E0")}),-1.0]])]});
            var Q1;
            Q1=makeQuery(id+"F0.imprint","IMPRINT",FACE,{"disambiguationData":[TD([[makeQuery(id+"F0.imprint","IMPRINT",EDGE,{"derivedFrom":sQuery(id+"F0.wireOp",EDGE,"E2")}),-1.0]])]});
            var Q2;
            Q2=makeQuery(id+"F0.imprint","IMPRINT",FACE,{"disambiguationData":[TD([[makeQuery(id+"F0.imprint","IMPRINT",EDGE,{"derivedFrom":sQuery(id+"F0.wireOp",EDGE,"E7")}),-1.0]])]});
            var Q3;
            Q3=makeQuery(id+"F0.imprint","IMPRINT",FACE,{"disambiguationData":[TD([[makeQuery(id+"F0.imprint","IMPRINT",EDGE,{"derivedFrom":sQuery(id+"F0.wireOp",EDGE,"E4")}),-1.0]])]});
            var Q4;
            Q4=makeQuery(id+"F0.imprint","IMPRINT",FACE,{"disambiguationData":[TD([[makeQuery(id+"F0.imprint","IMPRINT",EDGE,{"derivedFrom":sQuery(id+"F0.wireOp",EDGE,"E35")}),1.0]])]});
            var Q5;
            Q5=makeQuery(id+"F0.imprint","IMPRINT",FACE,{"disambiguationData":[TD([[makeQuery(id+"F0.imprint","IMPRINT",EDGE,{"derivedFrom":sQuery(id+"F0.wireOp",EDGE,"E19")}),-1.0]])]});
            var Q6;
            Q6=makeQuery(id+"F0.imprint","IMPRINT",FACE,{"disambiguationData":[TD([[makeQuery(id+"F0.imprint","IMPRINT",EDGE,{"derivedFrom":sQuery(id+"F0.wireOp",EDGE,"E9")}),-1.0]])]});
            extrude(context, id + "F1", {"entities" : qUnion([Q0, Q1, Q2, Q3, Q4, Q5, Q6]), "depth" : 3.17 * mm, "offsetDistance" : 25.4 * mm});
        }
        {
            var Q0;
            Q0=makeQuery(id+"F0.imprint","IMPRINT",FACE,{"disambiguationData":[TD([[makeQuery(id+"F0.imprint","IMPRINT",EDGE,{"derivedFrom":sQuery(id+"F0.wireOp",EDGE,"E13")}),1.0]])]});
            var Q1;
            Q1=makeQuery(id+"F0.imprint","IMPRINT",FACE,{"disambiguationData":[TD([[makeQuery(id+"F0.imprint","IMPRINT",EDGE,{"derivedFrom":sQuery(id+"F0.wireOp",EDGE,"E11")}),-1.0]])]});
            var Q2;
            Q2=makeQuery(id+"F0.imprint","IMPRINT",FACE,{"disambiguationData":[TD([[makeQuery(id+"F0.imprint","IMPRINT",EDGE,{"derivedFrom":sQuery(id+"F0.wireOp",EDGE,"E23")}),-1.0]])]});
            var Q3;
            Q3=makeQuery(id+"F0.imprint","IMPRINT",FACE,{"disambiguationData":[TD([[makeQuery(id+"F0.imprint","IMPRINT",EDGE,{"derivedFrom":sQuery(id+"F0.wireOp",EDGE,"E31")}),-1.0]])]});
            var Q4;
            Q4=makeQuery(id+"F0.imprint","IMPRINT",FACE,{"disambiguationData":[TD([[makeQuery(id+"F0.imprint","IMPRINT",EDGE,{"derivedFrom":sQuery(id+"F0.wireOp",EDGE,"E17")}),-1.0]])]});
            var Q5;
            Q5=makeQuery(id+"F0.imprint","IMPRINT",FACE,{"disambiguationData":[TD([[makeQuery(id+"F0.imprint","IMPRINT",EDGE,{"derivedFrom":sQuery(id+"F0.wireOp",EDGE,"E21")}),-1.0]])]});
            var Q6;
            Q6=makeQuery(id+"F0.imprint","IMPRINT",FACE,{"disambiguationData":[TD([[makeQuery(id+"F0.imprint","IMPRINT",EDGE,{"derivedFrom":sQuery(id+"F0.wireOp",EDGE,"E9")}),1.0]])]});
            var Q7;
            Q7=makeQuery(id+"F0.imprint","IMPRINT",FACE,{"disambiguationData":[TD([[makeQuery(id+"F0.imprint","IMPRINT",EDGE,{"derivedFrom":sQuery(id+"F0.wireOp",EDGE,"E29")}),-1.0]])]});
            extrude(context, id + "F2", {"entities" : qUnion([Q0, Q1, Q2, Q3, Q4, Q5, Q6, Q7]), "depth" : 3.56 * mm, "offsetDistance" : 25.4 * mm});
        }
        {
            var Q0;
            Q0=makeQuery(id+"F0.imprint","IMPRINT",FACE,{"disambiguationData":[TD([[makeQuery(id+"F0.imprint","IMPRINT",EDGE,{"derivedFrom":sQuery(id+"F0.wireOp",EDGE,"E111")}),1.0]])]});
            var Q1;
            Q1=makeQuery(id+"F0.imprint","IMPRINT",FACE,{"disambiguationData":[TD([[makeQuery(id+"F0.imprint","IMPRINT",EDGE,{"derivedFrom":sQuery(id+"F0.wireOp",EDGE,"E145")}),1.0]])]});
            var Q2;
            Q2=makeQuery(id+"F0.imprint","IMPRINT",FACE,{"disambiguationData":[TD([[makeQuery(id+"F0.imprint","IMPRINT",EDGE,{"derivedFrom":sQuery(id+"F0.wireOp",EDGE,"E112")}),1.0]])]});
            var Q3;
            Q3=makeQuery(id+"F0.imprint","IMPRINT",FACE,{"disambiguationData":[TD([[makeQuery(id+"F0.imprint","IMPRINT",EDGE,{"derivedFrom":sQuery(id+"F0.wireOp",EDGE,"E148")}),1.0]])]});
            var Q4;
            Q4=makeQuery(id+"F0.imprint","IMPRINT",FACE,{"disambiguationData":[TD([[makeQuery(id+"F0.imprint","IMPRINT",EDGE,{"derivedFrom":sQuery(id+"F0.wireOp",EDGE,"E144")}),1.0]])]});
            var Q5;
            Q5=makeQuery(id+"F0.imprint","IMPRINT",FACE,{"disambiguationData":[TD([[makeQuery(id+"F0.imprint","IMPRINT",EDGE,{"derivedFrom":sQuery(id+"F0.wireOp",EDGE,"E151")}),-1.0]])]});
            var Q6;
            {var subQ1=sQuery(id+"F0.wireOp",EDGE,"E141");Q6=makeQuery(id+"F0.imprint","IMPRINT",FACE,{"disambiguationData":[TD([[makeQuery(id+"F0.imprint","IMPRINT",EDGE,{"derivedFrom":subQ1}),-1.0]])]});}
            var Q7;
            Q7=makeQuery(id+"F0.imprint","IMPRINT",FACE,{"disambiguationData":[TD([[makeQuery(id+"F0.imprint","IMPRINT",EDGE,{"derivedFrom":sQuery(id+"F0.wireOp",EDGE,"E153")}),-1.0]])]});
            var Q8;
            {var subQ9=sQuery(id+"F0.wireOp",EDGE,"E128");Q8=makeQuery(id+"F0.imprint","IMPRINT",FACE,{"disambiguationData":[TD([[makeQuery(id+"F0.imprint","IMPRINT",EDGE,{"derivedFrom":subQ9}),1.0]])]});}
            var Q9;
            Q9=makeQuery(id+"F0.imprint","IMPRINT",FACE,{"disambiguationData":[TD([[makeQuery(id+"F0.imprint","IMPRINT",EDGE,{"derivedFrom":sQuery(id+"F0.wireOp",EDGE,"E79")}),-1.0]])]});
            var Q10;
            Q10=makeQuery(id+"F0.imprint","IMPRINT",FACE,{"disambiguationData":[TD([[makeQuery(id+"F0.imprint","IMPRINT",EDGE,{"derivedFrom":sQuery(id+"F0.wireOp",EDGE,"E99")}),-1.0]])]});
            var Q11;
            Q11=makeQuery(id+"F0.imprint","IMPRINT",FACE,{"disambiguationData":[TD([[makeQuery(id+"F0.imprint","IMPRINT",EDGE,{"derivedFrom":sQuery(id+"F0.wireOp",EDGE,"E96")}),1.0]])]});
            var Q12;
            Q12=makeQuery(id+"F0.imprint","IMPRINT",FACE,{"disambiguationData":[TD([[makeQuery(id+"F0.imprint","IMPRINT",EDGE,{"derivedFrom":sQuery(id+"F0.wireOp",EDGE,"E93")}),1.0]])]});
            var Q13;
            Q13=makeQuery(id+"F0.imprint","IMPRINT",FACE,{"disambiguationData":[TD([[makeQuery(id+"F0.imprint","IMPRINT",EDGE,{"derivedFrom":sQuery(id+"F0.wireOp",EDGE,"E90")}),1.0]])]});
            var Q14;
            Q14=makeQuery(id+"F0.imprint","IMPRINT",FACE,{"disambiguationData":[TD([[makeQuery(id+"F0.imprint","IMPRINT",EDGE,{"derivedFrom":sQuery(id+"F0.wireOp",EDGE,"E38")}),-1.0]])]});
            var Q15;
            Q15=makeQuery(id+"F0.imprint","IMPRINT",FACE,{"disambiguationData":[TD([[makeQuery(id+"F0.imprint","IMPRINT",EDGE,{"derivedFrom":sQuery(id+"F0.wireOp",EDGE,"E43")}),1.0]])]});
            var Q16;
            Q16=makeQuery(id+"F0.imprint","IMPRINT",FACE,{"disambiguationData":[TD([[makeQuery(id+"F0.imprint","IMPRINT",EDGE,{"derivedFrom":sQuery(id+"F0.wireOp",EDGE,"E74")}),1.0]])]});
            var Q17;
            Q17=makeQuery(id+"F0.imprint","IMPRINT",FACE,{"disambiguationData":[TD([[makeQuery(id+"F0.imprint","IMPRINT",EDGE,{"derivedFrom":sQuery(id+"F0.wireOp",EDGE,"E65")}),-1.0]])]});
            var Q18;
            Q18=makeQuery(id+"F0.imprint","IMPRINT",FACE,{"disambiguationData":[TD([[makeQuery(id+"F0.imprint","IMPRINT",EDGE,{"derivedFrom":sQuery(id+"F0.wireOp",EDGE,"E209")}),1.0]])]});
            var Q19;
            Q19=makeQuery(id+"F0.imprint","IMPRINT",FACE,{"disambiguationData":[TD([[makeQuery(id+"F0.imprint","IMPRINT",EDGE,{"derivedFrom":sQuery(id+"F0.wireOp",EDGE,"E170")}),1.0]])]});
            var Q20;
            {var subQ0=sQuery(id+"F0.wireOp",EDGE,"E196");Q20=makeQuery(id+"F0.imprint","IMPRINT",FACE,{"disambiguationData":[TD([[makeQuery(id+"F0.imprint","IMPRINT",EDGE,{"derivedFrom":subQ0}),1.0]])]});}
            var Q21;
            Q21=makeQuery(id+"F0.imprint","IMPRINT",FACE,{"disambiguationData":[TD([[makeQuery(id+"F0.imprint","IMPRINT",EDGE,{"derivedFrom":sQuery(id+"F0.wireOp",EDGE,"E166")}),1.0]])]});
            var Q22;
            Q22=makeQuery(id+"F0.imprint","IMPRINT",FACE,{"disambiguationData":[TD([[makeQuery(id+"F0.imprint","IMPRINT",EDGE,{"derivedFrom":sQuery(id+"F0.wireOp",EDGE,"E162")}),1.0]])]});
            var Q23;
            {var subQ2=sQuery(id+"F0.wireOp",EDGE,"E191");Q23=makeQuery(id+"F0.imprint","IMPRINT",FACE,{"disambiguationData":[TD([[makeQuery(id+"F0.imprint","IMPRINT",EDGE,{"derivedFrom":subQ2}),1.0]])]});}
            var Q24;
            Q24=makeQuery(id+"F0.imprint","IMPRINT",FACE,{"disambiguationData":[TD([[makeQuery(id+"F0.imprint","IMPRINT",EDGE,{"derivedFrom":sQuery(id+"F0.wireOp",EDGE,"E183")}),1.0]])]});
            var Q25;
            Q25=makeQuery(id+"F0.imprint","IMPRINT",FACE,{"disambiguationData":[TD([[makeQuery(id+"F0.imprint","IMPRINT",EDGE,{"derivedFrom":sQuery(id+"F0.wireOp",EDGE,"E188")}),1.0]])]});
            var Q26;
            {var subQ6=sQuery(id+"F0.wireOp",EDGE,"E181");Q26=makeQuery(id+"F0.imprint","IMPRINT",FACE,{"disambiguationData":[TD([[makeQuery(id+"F0.imprint","IMPRINT",EDGE,{"derivedFrom":subQ6}),1.0]])]});}
            var Q27;
            Q27=makeQuery(id+"F0.imprint","IMPRINT",FACE,{"disambiguationData":[TD([[makeQuery(id+"F0.imprint","IMPRINT",EDGE,{"derivedFrom":sQuery(id+"F0.wireOp",EDGE,"E48")}),1.0]])]});
            extrude(context, id + "F3", {"entities" : qUnion([Q0, Q1, Q2, Q3, Q4, Q5, Q6, Q7, Q8, Q9, Q10, Q11, Q12, Q13, Q14, Q15, Q16, Q17, Q18, Q19, Q20, Q21, Q22, Q23, Q24, Q25, Q26, Q27]), "depth" : 4.57 * mm, "offsetDistance" : 25.4 * mm});
        }
        {
            var Q0;
            Q0=makeQuery(id+"F0.imprint","IMPRINT",FACE,{"disambiguationData":[TD([[makeQuery(id+"F0.imprint","IMPRINT",EDGE,{"derivedFrom":sQuery(id+"F0.wireOp",EDGE,"E181")}),-1.0]])]});
            var Q1;
            {var subQ0=sQuery(id+"F0.wireOp",EDGE,"E263");Q1=makeQuery(id+"F0.imprint","IMPRINT",FACE,{"disambiguationData":[TD([[makeQuery(id+"F0.imprint","IMPRINT",EDGE,{"derivedFrom":subQ0}),1.0]])]});}
            var Q2;
            Q2=makeQuery(id+"F0.imprint","IMPRINT",FACE,{"disambiguationData":[TD([[makeQuery(id+"F0.imprint","IMPRINT",EDGE,{"derivedFrom":sQuery(id+"F0.wireOp",EDGE,"E182")}),1.0]])]});
            var Q3;
            {var subQ0=sQuery(id+"F0.wireOp",EDGE,"E264");Q3=makeQuery(id+"F0.imprint","IMPRINT",FACE,{"disambiguationData":[TD([[makeQuery(id+"F0.imprint","IMPRINT",EDGE,{"derivedFrom":subQ0}),1.0]])]});}
            var Q4;
            Q4=makeQuery(id+"F0.imprint","IMPRINT",FACE,{"disambiguationData":[TD([[makeQuery(id+"F0.imprint","IMPRINT",EDGE,{"derivedFrom":sQuery(id+"F0.wireOp",EDGE,"E184")}),-1.0]])]});
            var Q5;
            Q5=makeQuery(id+"F0.imprint","IMPRINT",FACE,{"disambiguationData":[TD([[makeQuery(id+"F0.imprint","IMPRINT",EDGE,{"derivedFrom":sQuery(id+"F0.wireOp",EDGE,"E183")}),-1.0]])]});
            var Q6;
            Q6=makeQuery(id+"F0.imprint","IMPRINT",FACE,{"disambiguationData":[TD([[makeQuery(id+"F0.imprint","IMPRINT",EDGE,{"derivedFrom":sQuery(id+"F0.wireOp",EDGE,"E185")}),1.0]])]});
            var Q7;
            Q7=makeQuery(id+"F0.imprint","IMPRINT",FACE,{"disambiguationData":[TD([[makeQuery(id+"F0.imprint","IMPRINT",EDGE,{"derivedFrom":sQuery(id+"F0.wireOp",EDGE,"E186")}),1.0]])]});
            var Q8;
            Q8=makeQuery(id+"F0.imprint","IMPRINT",FACE,{"disambiguationData":[TD([[makeQuery(id+"F0.imprint","IMPRINT",EDGE,{"derivedFrom":sQuery(id+"F0.wireOp",EDGE,"E187")}),-1.0]])]});
            var Q9;
            Q9=makeQuery(id+"F0.imprint","IMPRINT",FACE,{"disambiguationData":[TD([[makeQuery(id+"F0.imprint","IMPRINT",EDGE,{"derivedFrom":sQuery(id+"F0.wireOp",EDGE,"E190")}),1.0]])]});
            var Q10;
            Q10=makeQuery(id+"F0.imprint","IMPRINT",FACE,{"disambiguationData":[TD([[makeQuery(id+"F0.imprint","IMPRINT",EDGE,{"derivedFrom":sQuery(id+"F0.wireOp",EDGE,"E188")}),-1.0]])]});
            var Q11;
            Q11=makeQuery(id+"F0.imprint","IMPRINT",FACE,{"disambiguationData":[TD([[makeQuery(id+"F0.imprint","IMPRINT",EDGE,{"derivedFrom":sQuery(id+"F0.wireOp",EDGE,"E202")}),1.0]])]});
            var Q12;
            Q12=makeQuery(id+"F0.imprint","IMPRINT",FACE,{"disambiguationData":[TD([[makeQuery(id+"F0.imprint","IMPRINT",EDGE,{"derivedFrom":sQuery(id+"F0.wireOp",EDGE,"E204")}),-1.0]])]});
            var Q13;
            Q13=makeQuery(id+"F0.imprint","IMPRINT",FACE,{"disambiguationData":[TD([[makeQuery(id+"F0.imprint","IMPRINT",EDGE,{"derivedFrom":sQuery(id+"F0.wireOp",EDGE,"E203")}),-1.0]])]});
            var Q14;
            Q14=makeQuery(id+"F0.imprint","IMPRINT",FACE,{"disambiguationData":[TD([[makeQuery(id+"F0.imprint","IMPRINT",EDGE,{"derivedFrom":sQuery(id+"F0.wireOp",EDGE,"E198")}),-1.0]])]});
            var Q15;
            {var subQ0=sQuery(id+"F0.wireOp",EDGE,"E238");Q15=makeQuery(id+"F0.imprint","IMPRINT",FACE,{"disambiguationData":[TD([[makeQuery(id+"F0.imprint","IMPRINT",EDGE,{"derivedFrom":subQ0}),1.0]])]});}
            var Q16;
            Q16=makeQuery(id+"F0.imprint","IMPRINT",FACE,{"disambiguationData":[TD([[makeQuery(id+"F0.imprint","IMPRINT",EDGE,{"derivedFrom":sQuery(id+"F0.wireOp",EDGE,"E201")}),1.0]])]});
            var Q17;
            {var subQ0=sQuery(id+"F0.wireOp",EDGE,"E239");Q17=makeQuery(id+"F0.imprint","IMPRINT",FACE,{"disambiguationData":[TD([[makeQuery(id+"F0.imprint","IMPRINT",EDGE,{"derivedFrom":subQ0}),1.0]])]});}
            var Q18;
            {var subQ0=sQuery(id+"F0.wireOp",EDGE,"E265");var subQ1=sQuery(id+"F0.wireOp",EDGE,"E179");var subQ3=makeQuery(id+"F0.imprint","INTERSECT",VERTEX,{"derivedFrom":[subQ1,subQ0]});Q18=makeQuery(id+"F0.imprint","IMPRINT",FACE,{"disambiguationData":[TD([[makeQuery(id+"F0.imprint","IMPRINT",EDGE,{"disambiguationData":[TD([[subQ3,-1.0]])],"derivedFrom":subQ1}),-1.0]])]});}
            var Q19;
            Q19=makeQuery(id+"F0.imprint","IMPRINT",FACE,{"disambiguationData":[TD([[makeQuery(id+"F0.imprint","IMPRINT",EDGE,{"derivedFrom":sQuery(id+"F0.wireOp",EDGE,"E177")}),1.0]])]});
            var Q20;
            Q20=makeQuery(id+"F0.imprint","IMPRINT",FACE,{"disambiguationData":[TD([[makeQuery(id+"F0.imprint","IMPRINT",EDGE,{"derivedFrom":sQuery(id+"F0.wireOp",EDGE,"E178")}),1.0]])]});
            var Q21;
            Q21=makeQuery(id+"F0.imprint","IMPRINT",FACE,{"disambiguationData":[TD([[makeQuery(id+"F0.imprint","IMPRINT",EDGE,{"derivedFrom":sQuery(id+"F0.wireOp",EDGE,"E192")}),1.0]])]});
            var Q22;
            {var subQ0=sQuery(id+"F0.wireOp",EDGE,"E247");Q22=makeQuery(id+"F0.imprint","IMPRINT",FACE,{"disambiguationData":[TD([[makeQuery(id+"F0.imprint","IMPRINT",EDGE,{"derivedFrom":subQ0}),-1.0]])]});}
            var Q23;
            Q23=makeQuery(id+"F0.imprint","IMPRINT",FACE,{"disambiguationData":[TD([[makeQuery(id+"F0.imprint","IMPRINT",EDGE,{"derivedFrom":sQuery(id+"F0.wireOp",EDGE,"E208")}),1.0]])]});
            var Q24;
            Q24=makeQuery(id+"F0.imprint","IMPRINT",FACE,{"disambiguationData":[TD([[makeQuery(id+"F0.imprint","IMPRINT",EDGE,{"derivedFrom":sQuery(id+"F0.wireOp",EDGE,"E191")}),-1.0]])]});
            var Q25;
            Q25=makeQuery(id+"F0.imprint","IMPRINT",FACE,{"disambiguationData":[TD([[makeQuery(id+"F0.imprint","IMPRINT",EDGE,{"derivedFrom":sQuery(id+"F0.wireOp",EDGE,"E189")}),-1.0]])]});
            var Q26;
            Q26=makeQuery(id+"F0.imprint","IMPRINT",FACE,{"disambiguationData":[TD([[makeQuery(id+"F0.imprint","IMPRINT",EDGE,{"derivedFrom":sQuery(id+"F0.wireOp",EDGE,"E196")}),-1.0]])]});
            var Q27;
            Q27=makeQuery(id+"F0.imprint","IMPRINT",FACE,{"disambiguationData":[TD([[makeQuery(id+"F0.imprint","IMPRINT",EDGE,{"derivedFrom":sQuery(id+"F0.wireOp",EDGE,"E195")}),-1.0]])]});
            var Q28;
            Q28=makeQuery(id+"F0.imprint","IMPRINT",FACE,{"disambiguationData":[TD([[makeQuery(id+"F0.imprint","IMPRINT",EDGE,{"derivedFrom":sQuery(id+"F0.wireOp",EDGE,"E194")}),1.0]])]});
            var Q29;
            Q29=makeQuery(id+"F0.imprint","IMPRINT",FACE,{"disambiguationData":[TD([[makeQuery(id+"F0.imprint","IMPRINT",EDGE,{"derivedFrom":sQuery(id+"F0.wireOp",EDGE,"E206")}),1.0]])]});
            var Q30;
            Q30=makeQuery(id+"F0.imprint","IMPRINT",FACE,{"disambiguationData":[TD([[makeQuery(id+"F0.imprint","IMPRINT",EDGE,{"derivedFrom":sQuery(id+"F0.wireOp",EDGE,"E207")}),-1.0]])]});
            var Q31;
            {var subQ0=sQuery(id+"F0.wireOp",EDGE,"E252");var subQ1=sQuery(id+"F0.wireOp",EDGE,"E205");var subQ3=makeQuery(id+"F0.imprint","INTERSECT",VERTEX,{"derivedFrom":[subQ1,subQ0]});Q31=makeQuery(id+"F0.imprint","IMPRINT",FACE,{"disambiguationData":[TD([[makeQuery(id+"F0.imprint","IMPRINT",EDGE,{"disambiguationData":[TD([[subQ3,1.0]])],"derivedFrom":subQ1}),-1.0]])]});}
            var Q32;
            Q32=makeQuery(id+"F0.imprint","IMPRINT",FACE,{"disambiguationData":[TD([[makeQuery(id+"F0.imprint","IMPRINT",EDGE,{"derivedFrom":sQuery(id+"F0.wireOp",EDGE,"zbWgLwIs-3z88-qguG-AInn-ASTAg1sW55JD")}),-1.0]])]});
            var Q33;
            Q33=makeQuery(id+"F0.imprint","IMPRINT",FACE,{"disambiguationData":[TD([[makeQuery(id+"F0.imprint","IMPRINT",EDGE,{"derivedFrom":sQuery(id+"F0.wireOp",EDGE,"XdCiT3gj-7MIM-V4Jr-JYmO-7Q9DVdCq5Ljk")}),1.0]])]});
            var Q34;
            Q34=makeQuery(id+"F0.imprint","IMPRINT",FACE,{"disambiguationData":[TD([[makeQuery(id+"F0.imprint","IMPRINT",EDGE,{"derivedFrom":sQuery(id+"F0.wireOp",EDGE,"E57")}),1.0]])]});
            var Q35;
            Q35=makeQuery(id+"F0.imprint","IMPRINT",FACE,{"disambiguationData":[TD([[makeQuery(id+"F0.imprint","IMPRINT",EDGE,{"derivedFrom":sQuery(id+"F0.wireOp",EDGE,"E138")}),1.0]])]});
            var Q36;
            Q36=makeQuery(id+"F0.imprint","IMPRINT",FACE,{"disambiguationData":[TD([[makeQuery(id+"F0.imprint","IMPRINT",EDGE,{"derivedFrom":sQuery(id+"F0.wireOp",EDGE,"E137")}),1.0]])]});
            var Q37;
            Q37=makeQuery(id+"F0.imprint","IMPRINT",FACE,{"disambiguationData":[TD([[makeQuery(id+"F0.imprint","IMPRINT",EDGE,{"derivedFrom":sQuery(id+"F0.wireOp",EDGE,"E147")}),-1.0]])]});
            var Q38;
            {var subQ0=sQuery(id+"F0.wireOp",EDGE,"E228");Q38=makeQuery(id+"F0.imprint","IMPRINT",FACE,{"disambiguationData":[TD([[makeQuery(id+"F0.imprint","IMPRINT",EDGE,{"derivedFrom":subQ0}),-1.0]])]});}
            var Q39;
            {var subQ0=sQuery(id+"F0.wireOp",EDGE,"E227");Q39=makeQuery(id+"F0.imprint","IMPRINT",FACE,{"disambiguationData":[TD([[makeQuery(id+"F0.imprint","IMPRINT",EDGE,{"derivedFrom":subQ0}),-1.0]])]});}
            var Q40;
            {var subQ0=sQuery(id+"F0.wireOp",EDGE,"E226");Q40=makeQuery(id+"F0.imprint","IMPRINT",FACE,{"disambiguationData":[TD([[makeQuery(id+"F0.imprint","IMPRINT",EDGE,{"derivedFrom":subQ0}),-1.0]])]});}
            var Q41;
            Q41=makeQuery(id+"F0.imprint","IMPRINT",FACE,{"disambiguationData":[TD([[makeQuery(id+"F0.imprint","IMPRINT",EDGE,{"derivedFrom":sQuery(id+"F0.wireOp",EDGE,"E139")}),1.0]])]});
            var Q42;
            Q42=makeQuery(id+"F0.imprint","IMPRINT",FACE,{"disambiguationData":[TD([[makeQuery(id+"F0.imprint","IMPRINT",EDGE,{"derivedFrom":sQuery(id+"F0.wireOp",EDGE,"E140")}),1.0]])]});
            var Q43;
            Q43=makeQuery(id+"F0.imprint","IMPRINT",FACE,{"disambiguationData":[TD([[makeQuery(id+"F0.imprint","IMPRINT",EDGE,{"derivedFrom":sQuery(id+"F0.wireOp",EDGE,"E153")}),1.0]])]});
            var Q44;
            Q44=makeQuery(id+"F0.imprint","IMPRINT",FACE,{"disambiguationData":[TD([[makeQuery(id+"F0.imprint","IMPRINT",EDGE,{"derivedFrom":sQuery(id+"F0.wireOp",EDGE,"E141")}),1.0]])]});
            var Q45;
            {var subQ0=sQuery(id+"F0.wireOp",EDGE,"E212");Q45=makeQuery(id+"F0.imprint","IMPRINT",FACE,{"disambiguationData":[TD([[makeQuery(id+"F0.imprint","IMPRINT",EDGE,{"derivedFrom":subQ0}),-1.0]])]});}
            var Q46;
            Q46=makeQuery(id+"F0.imprint","IMPRINT",FACE,{"disambiguationData":[TD([[makeQuery(id+"F0.imprint","IMPRINT",EDGE,{"derivedFrom":sQuery(id+"F0.wireOp",EDGE,"E150")}),1.0]])]});
            var Q47;
            {var subQ0=sQuery(id+"F0.wireOp",EDGE,"E214");Q47=makeQuery(id+"F0.imprint","IMPRINT",FACE,{"disambiguationData":[TD([[makeQuery(id+"F0.imprint","IMPRINT",EDGE,{"derivedFrom":subQ0}),1.0]])]});}
            var Q48;
            {var subQ0=sQuery(id+"F0.wireOp",EDGE,"E216");Q48=makeQuery(id+"F0.imprint","IMPRINT",FACE,{"disambiguationData":[TD([[makeQuery(id+"F0.imprint","IMPRINT",EDGE,{"derivedFrom":subQ0}),-1.0]])]});}
            var Q49;
            Q49=makeQuery(id+"F0.imprint","IMPRINT",FACE,{"disambiguationData":[TD([[makeQuery(id+"F0.imprint","IMPRINT",EDGE,{"derivedFrom":sQuery(id+"F0.wireOp",EDGE,"E156")}),-1.0]])]});
            var Q50;
            Q50=makeQuery(id+"F0.imprint","IMPRINT",FACE,{"disambiguationData":[TD([[makeQuery(id+"F0.imprint","IMPRINT",EDGE,{"derivedFrom":sQuery(id+"F0.wireOp",EDGE,"E144")}),-1.0]])]});
            var Q51;
            Q51=makeQuery(id+"F0.imprint","IMPRINT",FACE,{"disambiguationData":[TD([[makeQuery(id+"F0.imprint","IMPRINT",EDGE,{"derivedFrom":sQuery(id+"F0.wireOp",EDGE,"E148")}),-1.0]])]});
            var Q52;
            Q52=makeQuery(id+"F0.imprint","IMPRINT",FACE,{"disambiguationData":[TD([[makeQuery(id+"F0.imprint","IMPRINT",EDGE,{"derivedFrom":sQuery(id+"F0.wireOp",EDGE,"E151")}),1.0]])]});
            var Q53;
            Q53=makeQuery(id+"F0.imprint","IMPRINT",FACE,{"disambiguationData":[TD([[makeQuery(id+"F0.imprint","IMPRINT",EDGE,{"derivedFrom":sQuery(id+"F0.wireOp",EDGE,"E152")}),-1.0]])]});
            var Q54;
            Q54=makeQuery(id+"F0.imprint","IMPRINT",FACE,{"disambiguationData":[TD([[makeQuery(id+"F0.imprint","IMPRINT",EDGE,{"derivedFrom":sQuery(id+"F0.wireOp",EDGE,"E149")}),1.0]])]});
            var Q55;
            Q55=makeQuery(id+"F0.imprint","IMPRINT",FACE,{"disambiguationData":[TD([[makeQuery(id+"F0.imprint","IMPRINT",EDGE,{"derivedFrom":sQuery(id+"F0.wireOp",EDGE,"E155")}),1.0]])]});
            var Q56;
            Q56=makeQuery(id+"F0.imprint","IMPRINT",FACE,{"disambiguationData":[TD([[makeQuery(id+"F0.imprint","IMPRINT",EDGE,{"derivedFrom":sQuery(id+"F0.wireOp",EDGE,"E154")}),-1.0]])]});
            var Q57;
            Q57=makeQuery(id+"F0.imprint","IMPRINT",FACE,{"disambiguationData":[TD([[makeQuery(id+"F0.imprint","IMPRINT",EDGE,{"derivedFrom":sQuery(id+"F0.wireOp",EDGE,"E146")}),-1.0]])]});
            var Q58;
            Q58=makeQuery(id+"F0.imprint","IMPRINT",FACE,{"disambiguationData":[TD([[makeQuery(id+"F0.imprint","IMPRINT",EDGE,{"derivedFrom":sQuery(id+"F0.wireOp",EDGE,"E268")}),-1.0]])]});
            var Q59;
            Q59=makeQuery(id+"F0.imprint","IMPRINT",FACE,{"disambiguationData":[TD([[makeQuery(id+"F0.imprint","IMPRINT",EDGE,{"derivedFrom":sQuery(id+"F0.wireOp",EDGE,"E272")}),-1.0]])]});
            extrude(context, id + "F4", {"entities" : qUnion([Q0, Q1, Q2, Q3, Q4, Q5, Q6, Q7, Q8, Q9, Q10, Q11, Q12, Q13, Q14, Q15, Q16, Q17, Q18, Q19, Q20, Q21, Q22, Q23, Q24, Q25, Q26, Q27, Q28, Q29, Q30, Q31, Q32, Q33, Q34, Q35, Q36, Q37, Q38, Q39, Q40, Q41, Q42, Q43, Q44, Q45, Q46, Q47, Q48, Q49, Q50, Q51, Q52, Q53, Q54, Q55, Q56, Q57, Q58, Q59]), "depth" : 5.08 * mm, "offsetDistance" : 25.4 * mm});
        }
        {
            var Q0;
            Q0=makeQuery(id+"F0.imprint","IMPRINT",FACE,{"disambiguationData":[TD([[makeQuery(id+"F0.imprint","IMPRINT",EDGE,{"derivedFrom":sQuery(id+"F0.wireOp",EDGE,"E110")}),1.0]])]});
            var Q1;
            Q1=makeQuery(id+"F0.imprint","IMPRINT",FACE,{"disambiguationData":[TD([[makeQuery(id+"F0.imprint","IMPRINT",EDGE,{"derivedFrom":sQuery(id+"F0.wireOp",EDGE,"E187")}),1.0]])]});
            extrude(context, id + "F5", {"entities" : qUnion([Q0, Q1]), "depth" : 4.57 * mm, "offsetDistance" : 25.4 * mm});
        }
        {
            var Q0;
            Q0=makeQuery(id+"F0.imprint","IMPRINT",FACE,{"disambiguationData":[TD([[makeQuery(id+"F0.imprint","IMPRINT",EDGE,{"derivedFrom":sQuery(id+"F0.wireOp",EDGE,"E103")}),-1.0]])]});
            var Q1;
            Q1=makeQuery(id+"F0.imprint","IMPRINT",FACE,{"disambiguationData":[TD([[makeQuery(id+"F0.imprint","IMPRINT",EDGE,{"derivedFrom":sQuery(id+"F0.wireOp",EDGE,"E157")}),-1.0]])]});
            extrude(context, id + "F6", {"entities" : qUnion([Q0, Q1]), "depth" : 4.57 * mm, "offsetDistance" : 25.4 * mm});
        }
    });
